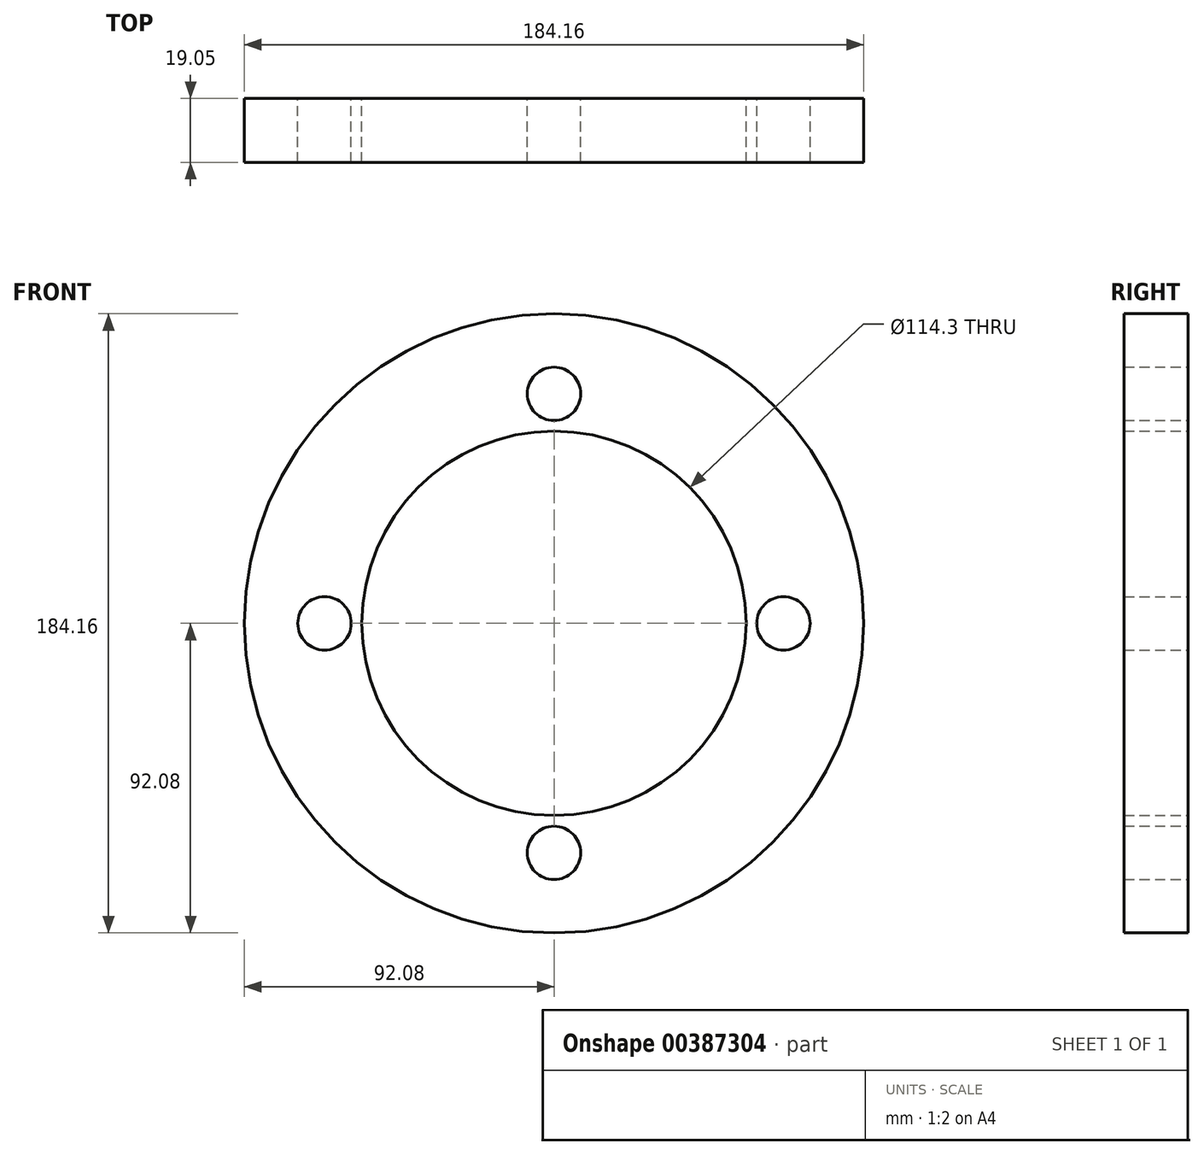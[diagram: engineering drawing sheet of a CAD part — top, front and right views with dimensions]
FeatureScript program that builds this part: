
annotation { "Feature Type Name" : "Feature", "Feature Type Description" : "" }
export const myFeature = defineFeature(function(context is Context, id is Id, definition is map)
    precondition{}
    {
        {
            var Q0;
            Q0=qCreatedBy(makeId("Front.planeOp"),FACE);
            var sketch = newSketch(context, id + "F0", { "sketchPlane" : qUnion([Q0])});
            skCircle(sketch, "E0", {"center": v(0, 0) * mm, "radius": 57.15 * mm});
            skCircle(sketch, "E1", {"center": v(0, 0) * mm, "radius": 92.08 * mm});
            skCircle(sketch, "E2", {"center": v(0, 68.26) * mm, "radius": 7.94 * mm});
            skCircle(sketch, "E3", {"center": v(0, 0) * mm, "radius": 68.26 * mm, "construction": true});
            skCircle(sketch, "E4.0.1.0", {"center": v(-68.26, 0) * mm, "radius": 7.94 * mm});
            skCircle(sketch, "E4.0.2.0", {"center": v(0, -68.26) * mm, "radius": 7.94 * mm});
            skCircle(sketch, "E4.0.3.0", {"center": v(68.26, 0) * mm, "radius": 7.94 * mm});
            skSolve(sketch);
        }
        {
            var Q0;
            Q0 = qSketchRegion(id + "F0", true);
            extrude(context, id + "F1", {"entities" : qUnion([Q0]), "flatOperationType" : FlatOperationType.REMOVE, "offsetDistance" : 25.4 * mm, "depth" : 19.05 * mm, "domain" : OperationDomain.MODEL});
        }
    });
